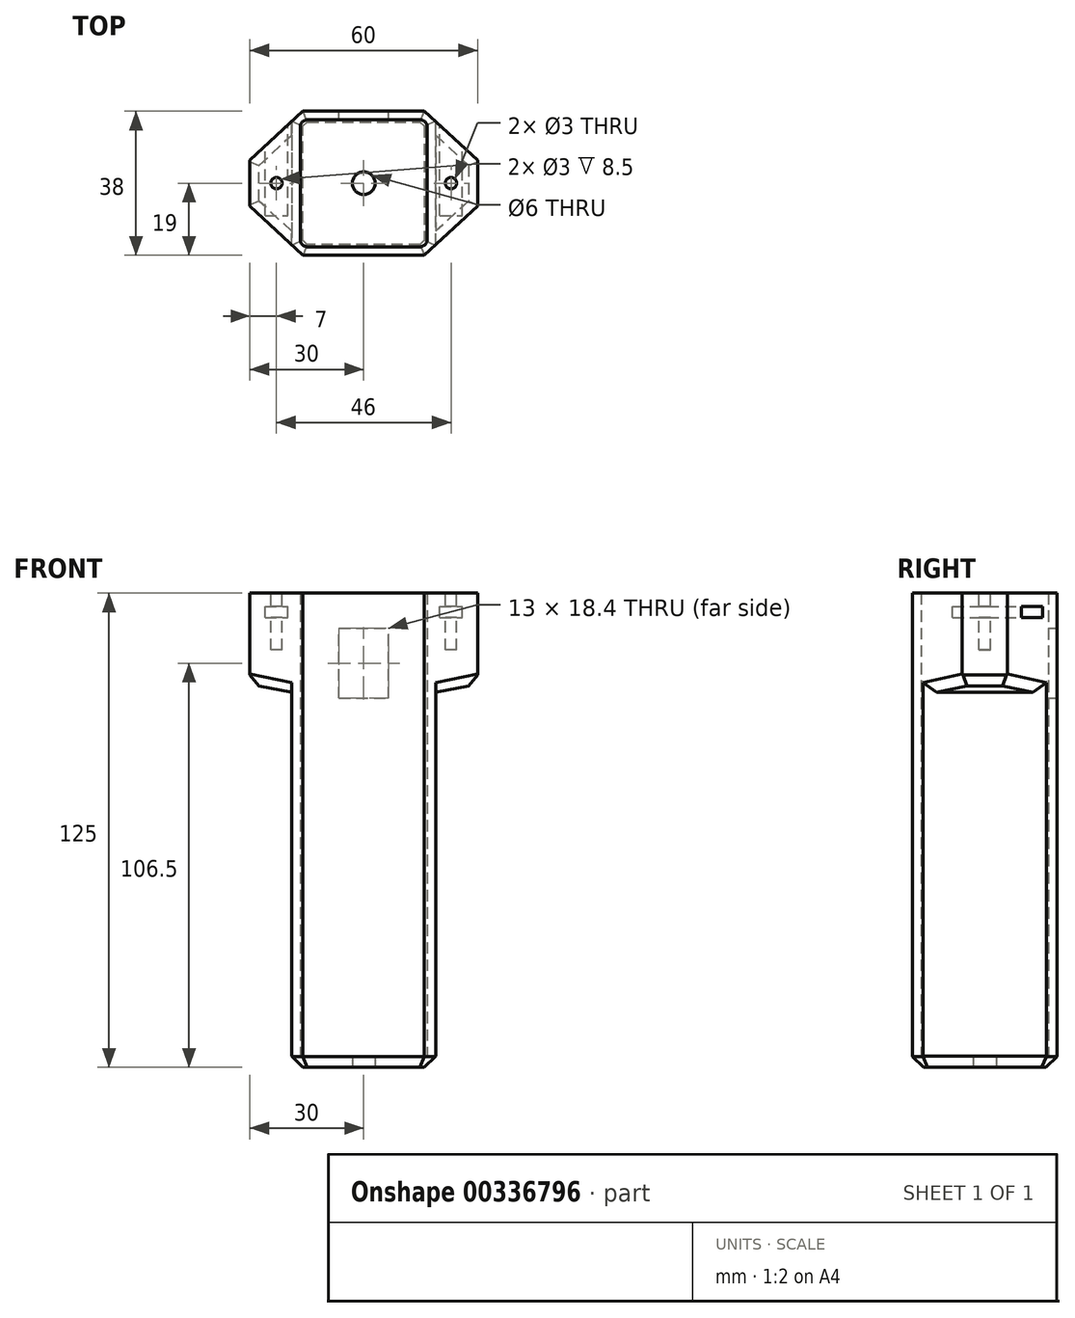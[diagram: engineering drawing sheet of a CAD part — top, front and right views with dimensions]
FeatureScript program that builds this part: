
annotation { "Feature Type Name" : "Feature", "Feature Type Description" : "" }
export const myFeature = defineFeature(function(context is Context, id is Id, definition is map)
    precondition{}
    {
        {
            var Q0;
            Q0=qCreatedBy(makeId("Top.planeOp"),FACE);
            var sketch = newSketch(context, id + "F0", { "sketchPlane" : qUnion([Q0])});
            skLineSegment(sketch, "E0.bottom", {"start": v(14.75, -16.75) * mm, "end": v(-14.75, -16.75) * mm});
            skLineSegment(sketch, "E0.top", {"start": v(14.75, 16.75) * mm, "end": v(-14.75, 16.75) * mm});
            skLineSegment(sketch, "E0.left", {"start": v(16.75, -14.75) * mm, "end": v(16.75, 14.75) * mm});
            skLineSegment(sketch, "E0.right", {"start": v(-16.75, -14.75) * mm, "end": v(-16.75, 14.75) * mm});
            skPoint(sketch, "E0.middle", {"position": v(0, 0) * mm});
            skLineSegment(sketch, "E1", {"start": v(-16, -19) * mm, "end": v(-30, -6) * mm});
            skLineSegment(sketch, "E2", {"start": v(-30, 6) * mm, "end": v(-16, 19) * mm});
            skLineSegment(sketch, "E3", {"start": v(16, 19) * mm, "end": v(30, 6) * mm});
            skLineSegment(sketch, "E4", {"start": v(30, -6) * mm, "end": v(16, -19) * mm});
            skLineSegment(sketch, "E5", {"start": v(-16, -19) * mm, "end": v(16, -19) * mm});
            skLineSegment(sketch, "E6", {"start": v(-30, -6) * mm, "end": v(-30, 6) * mm});
            skLineSegment(sketch, "E7", {"start": v(30, -6) * mm, "end": v(30, 6) * mm});
            skLineSegment(sketch, "E8", {"start": v(16, 19) * mm, "end": v(-16, 19) * mm});
            skPoint(sketch, "E9.visualSharp", {"position": v(-16.75, 16.75) * mm});
            skArc(sketch, "E9.filletArc", {"start": v(-14.75, 16.75) * mm, "mid": v(-16.16, 16.16) * mm, "end": v(-16.75, 14.75) * mm});
            skPoint(sketch, "E10.visualSharp", {"position": v(16.75, 16.75) * mm});
            skArc(sketch, "E10.filletArc", {"start": v(16.75, 14.75) * mm, "mid": v(16.16, 16.16) * mm, "end": v(14.75, 16.75) * mm});
            skPoint(sketch, "E11.visualSharp", {"position": v(16.75, -16.75) * mm});
            skArc(sketch, "E11.filletArc", {"start": v(14.75, -16.75) * mm, "mid": v(16.16, -16.16) * mm, "end": v(16.75, -14.75) * mm});
            skPoint(sketch, "E12.visualSharp", {"position": v(-16.75, -16.75) * mm});
            skArc(sketch, "E12.filletArc", {"start": v(-16.75, -14.75) * mm, "mid": v(-16.16, -16.16) * mm, "end": v(-14.75, -16.75) * mm});
            skSolve(sketch);
        }
        {
            var Q0;
            Q0 = qSketchRegion(id + "F0", true);
            extrude(context, id + "F1", {"entities" : qUnion([Q0]), "depth" : 115 * mm});
        }
        {
            var Q0;
            Q0=makeQuery(id+"F1.opExtrude","CAP_FACE",FACE,{"disambiguationData":[OSD([sQuery(id+"F0.wireOp",EDGE,"E0.bottom"),sQuery(id+"F0.wireOp",EDGE,"E0.top"),sQuery(id+"F0.wireOp",EDGE,"E0.left"),sQuery(id+"F0.wireOp",EDGE,"E0.right"),sQuery(id+"F0.wireOp",EDGE,"E1"),sQuery(id+"F0.wireOp",EDGE,"E2"),sQuery(id+"F0.wireOp",EDGE,"E3"),sQuery(id+"F0.wireOp",EDGE,"E4"),sQuery(id+"F0.wireOp",EDGE,"E5"),sQuery(id+"F0.wireOp",EDGE,"E6"),sQuery(id+"F0.wireOp",EDGE,"E7"),sQuery(id+"F0.wireOp",EDGE,"E8"),sQuery(id+"F0.wireOp",EDGE,"E9.filletArc"),sQuery(id+"F0.wireOp",EDGE,"E10.filletArc"),sQuery(id+"F0.wireOp",EDGE,"E11.filletArc"),sQuery(id+"F0.wireOp",EDGE,"E12.filletArc")])],"isStart":true});
            var sketch = newSketch(context, id + "F2", { "sketchPlane" : qUnion([Q0])});
            skLineSegment(sketch, "E13", {"start": v(16, 19) * mm, "end": v(30, 6) * mm});
            skLineSegment(sketch, "E14", {"start": v(30, 6) * mm, "end": v(30, -6) * mm});
            skLineSegment(sketch, "E15", {"start": v(30, -6) * mm, "end": v(16, -19) * mm});
            skLineSegment(sketch, "E16", {"start": v(16, -19) * mm, "end": v(-16, -19) * mm});
            skLineSegment(sketch, "E17", {"start": v(-16, -19) * mm, "end": v(-30, -6) * mm});
            skLineSegment(sketch, "E18", {"start": v(-30, -6) * mm, "end": v(-30, 6) * mm});
            skLineSegment(sketch, "E19", {"start": v(-30, 6) * mm, "end": v(-16, 19) * mm});
            skLineSegment(sketch, "E20", {"start": v(-16, 19) * mm, "end": v(16, 19) * mm});
            skSolve(sketch);
        }
        {
            var Q0;
            Q0 = qSketchRegion(id + "F2", true);
            var Q1;
            Q1 = qSketchRegion(id + "F4", true);
            extrude(context, id + "F3", {"entities" : qUnion([Q0, Q1]), "operationType" : NewBodyOperationType.ADD, "depth" : 10 * mm});
        }
        {
            var Q0;
            Q0=makeQuery(id+"F3.opExtrude","CAP_FACE",FACE,{"disambiguationData":[OSD([sQuery(id+"F2.wireOp",EDGE,"E13"),sQuery(id+"F2.wireOp",EDGE,"E14"),sQuery(id+"F2.wireOp",EDGE,"E15"),sQuery(id+"F2.wireOp",EDGE,"E16"),sQuery(id+"F2.wireOp",EDGE,"E17"),sQuery(id+"F2.wireOp",EDGE,"E18"),sQuery(id+"F2.wireOp",EDGE,"E19"),sQuery(id+"F2.wireOp",EDGE,"E20")])],"isStart":false});
            var sketch = newSketch(context, id + "F4", { "sketchPlane" : qUnion([Q0])});
            skCircle(sketch, "E21", {"center": v(0, 0) * mm, "radius": 3 * mm});
            skSolve(sketch);
        }
        {
            var Q0;
            Q0 = qSketchRegion(id + "F4", true);
            extrude(context, id + "F5", {"entities" : qUnion([Q0]), "operationType" : NewBodyOperationType.REMOVE, "oppositeDirection" : true, "depth" : 25 * mm});
        }
        {
            var Q0;
            Q0=makeQuery(id+"F1.opExtrude","CAP_FACE",FACE,{"disambiguationData":[OSD([sQuery(id+"F0.wireOp",EDGE,"E0.bottom"),sQuery(id+"F0.wireOp",EDGE,"E0.top"),sQuery(id+"F0.wireOp",EDGE,"E0.left"),sQuery(id+"F0.wireOp",EDGE,"E0.right"),sQuery(id+"F0.wireOp",EDGE,"E1"),sQuery(id+"F0.wireOp",EDGE,"E2"),sQuery(id+"F0.wireOp",EDGE,"E3"),sQuery(id+"F0.wireOp",EDGE,"E4"),sQuery(id+"F0.wireOp",EDGE,"E5"),sQuery(id+"F0.wireOp",EDGE,"E6"),sQuery(id+"F0.wireOp",EDGE,"E7"),sQuery(id+"F0.wireOp",EDGE,"E8"),sQuery(id+"F0.wireOp",EDGE,"E9.filletArc"),sQuery(id+"F0.wireOp",EDGE,"E10.filletArc"),sQuery(id+"F0.wireOp",EDGE,"E11.filletArc"),sQuery(id+"F0.wireOp",EDGE,"E12.filletArc")])],"isStart":false});
            var sketch = newSketch(context, id + "F6", { "sketchPlane" : qUnion([Q0])});
            skLineSegment(sketch, "E22", {"start": v(-30, -6) * mm, "end": v(-30, 6) * mm});
            skLineSegment(sketch, "E23", {"start": v(-30, 6) * mm, "end": v(-16, 19) * mm});
            skLineSegment(sketch, "E24", {"start": v(-16, 19) * mm, "end": v(16, 19) * mm});
            skLineSegment(sketch, "E25", {"start": v(16, 19) * mm, "end": v(30, 6) * mm});
            skLineSegment(sketch, "E26", {"start": v(30, 6) * mm, "end": v(30, -6) * mm});
            skLineSegment(sketch, "E27", {"start": v(30, -6) * mm, "end": v(16, -19) * mm});
            skLineSegment(sketch, "E28", {"start": v(16, -19) * mm, "end": v(-16, -19) * mm});
            skLineSegment(sketch, "E29", {"start": v(-16, -19) * mm, "end": v(-30, -6) * mm});
            skSolve(sketch);
        }
        {
            var Q0;
            Q0=makeQuery(id+"F6.imprint","IMPRINT",FACE,{"disambiguationData":[TD([[makeQuery(id+"F6.imprint","IMPRINT",EDGE,{"derivedFrom":sQuery(id+"F6.wireOp",EDGE,"E22")}),-1.0]])]});
            var sketch = newSketch(context, id + "F7", { "sketchPlane" : qUnion([Q0])});
            skPoint(sketch, "E30.middle", {"position": v(0, 0) * mm});
            skCircle(sketch, "E31", {"center": v(23, 0) * mm, "radius": 1.5 * mm});
            skCircle(sketch, "E32", {"center": v(-23, 0) * mm, "radius": 1.5 * mm});
            skLineSegment(sketch, "E33.bottom", {"start": v(-23, 0) * mm, "end": v(23, 0) * mm});
            skLineSegment(sketch, "E33.top", {"start": v(-23, 19.77) * mm, "end": v(23, 19.77) * mm});
            skLineSegment(sketch, "E33.left", {"start": v(-23, 0) * mm, "end": v(-23, 19.77) * mm});
            skLineSegment(sketch, "E33.right", {"start": v(23, 0) * mm, "end": v(23, 19.77) * mm});
            skSolve(sketch);
        }
        {
            var Q0;
            Q0=makeQuery(id+"F7.imprint","IMPRINT",FACE,{"disambiguationData":[TD([[makeQuery(id+"F7.imprint","IMPRINT",EDGE,{"derivedFrom":sQuery(id+"F7.wireOp",EDGE,"E31")}),1.0]])]});
            var Q1;
            Q1=makeQuery(id+"F7.imprint","IMPRINT",FACE,{"disambiguationData":[TD([[makeQuery(id+"F7.imprint","IMPRINT",EDGE,{"derivedFrom":sQuery(id+"F7.wireOp",EDGE,"E32")}),1.0]])]});
            var Q2;
            Q2=sQuery(id+"F7.wireOp",EDGE,"E31");
            var Q3;
            Q3=sQuery(id+"F7.wireOp",EDGE,"E32");
            extrude(context, id + "F8", {"entities" : qUnion([Q0, Q1]), "operationType" : NewBodyOperationType.REMOVE, "surfaceEntities" : qUnion([Q2, Q3]), "oppositeDirection" : true, "depth" : 15 * mm});
        }
        {
            var Q0;
            Q0=makeQuery(id+"F3.opExtrude","CAP_EDGE",EDGE,{"disambiguationData":[OSD([sQuery(id+"F2.wireOp",EDGE,"E16")])],"isStart":false});
            var Q1;
            Q1=makeQuery(id+"F3.opExtrude","CAP_EDGE",EDGE,{"disambiguationData":[OSD([sQuery(id+"F2.wireOp",EDGE,"E17")])],"isStart":false});
            var Q2;
            Q2=makeQuery(id+"F3.opExtrude","CAP_EDGE",EDGE,{"disambiguationData":[OSD([sQuery(id+"F2.wireOp",EDGE,"E15")])],"isStart":false});
            var Q3;
            Q3=makeQuery(id+"F3.opExtrude","CAP_EDGE",EDGE,{"disambiguationData":[OSD([sQuery(id+"F2.wireOp",EDGE,"E13")])],"isStart":false});
            var Q4;
            Q4=makeQuery(id+"F3.opExtrude","CAP_EDGE",EDGE,{"disambiguationData":[OSD([sQuery(id+"F2.wireOp",EDGE,"E20")])],"isStart":false});
            var Q5;
            Q5=makeQuery(id+"F3.opExtrude","CAP_EDGE",EDGE,{"disambiguationData":[OSD([sQuery(id+"F2.wireOp",EDGE,"E19")])],"isStart":false});
            var Q6;
            Q6=makeQuery(id+"F3.opExtrude","CAP_EDGE",EDGE,{"disambiguationData":[OSD([sQuery(id+"F2.wireOp",EDGE,"E18")])],"isStart":false});
            var Q7;
            Q7=makeQuery(id+"F3.opExtrude","CAP_EDGE",EDGE,{"disambiguationData":[OSD([sQuery(id+"F2.wireOp",EDGE,"E14")])],"isStart":false});
            chamfer(context, id + "F9", {"entities" : qUnion([Q0, Q1, Q2, Q3, Q4, Q5, Q6, Q7]), "width" : 2.9 * mm, "tangentPropagation" : true});
        }
        {
            var Q0;
            Q0=makeQuery(id+"F3.boolean.opBoolean","MERGE",FACE,{"derivedFrom":[makeQuery(id+"F1.opExtrude","SWEPT_FACE",FACE,{"disambiguationData":[OSD([sQuery(id+"F0.wireOp",EDGE,"E5")])]}),makeQuery(id+"F3.opExtrude","SWEPT_FACE",FACE,{"disambiguationData":[OSD([sQuery(id+"F2.wireOp",EDGE,"E20")])]})]});
            var sketch = newSketch(context, id + "F10", { "sketchPlane" : qUnion([Q0])});
            skLineSegment(sketch, "E34", {"start": v(0, 115) * mm, "end": v(0, 95) * mm});
            skPoint(sketch, "E34.endSnap0", {"position": v(0, 115) * mm});
            skPoint(sketch, "E35.middle", {"position": v(0, 95) * mm});
            skLineSegment(sketch, "E36", {"start": v(0, 85) * mm, "end": v(-50, 95) * mm});
            skLineSegment(sketch, "E37", {"start": v(0, 85) * mm, "end": v(50, 95) * mm});
            skPoint(sketch, "E38.middle", {"position": v(0, 85) * mm});
            skPoint(sketch, "E39.middle", {"position": v(12.9, 75) * mm});
            skLineSegment(sketch, "E40", {"start": v(19, 75) * mm, "end": v(19, 88.8) * mm});
            skLineSegment(sketch, "E41", {"start": v(-19, 75) * mm, "end": v(-19, 88.8) * mm});
            skLineSegment(sketch, "E42", {"start": v(19, 75) * mm, "end": v(19, -17.44) * mm});
            skLineSegment(sketch, "E43", {"start": v(-19, 75) * mm, "end": v(-19, -15.08) * mm});
            skLineSegment(sketch, "E44", {"start": v(-19, -15.08) * mm, "end": v(-58.81, -15.08) * mm});
            skLineSegment(sketch, "E45", {"start": v(-58.81, -15.08) * mm, "end": v(-73.57, 132.3) * mm});
            skLineSegment(sketch, "E46", {"start": v(58.57, 145.53) * mm, "end": v(83.51, 80.11) * mm});
            skLineSegment(sketch, "E47", {"start": v(83.51, 80.11) * mm, "end": v(61.9, -31.11) * mm});
            skLineSegment(sketch, "E48", {"start": v(61.9, -31.11) * mm, "end": v(19, -17.44) * mm});
            skLineSegment(sketch, "E49", {"start": v(-73.57, 132.3) * mm, "end": v(-50, 95) * mm});
            skLineSegment(sketch, "E50", {"start": v(50, 95) * mm, "end": v(58.57, 145.53) * mm});
            skSolve(sketch);
        }
        {
            var Q0;
            Q0 = qSketchRegion(id + "F10", true);
            extrude(context, id + "F11", {"entities" : qUnion([Q0]), "operationType" : NewBodyOperationType.REMOVE, "oppositeDirection" : true, "depth" : 50 * mm, "hasSecondDirection" : true, "secondDirectionOppositeDirection" : false, "secondDirectionDepth" : 25 * mm});
        }
        {
            var Q0;
            Q0=makeQuery(id+"F11.boolean.opBoolean","INTERSECT",EDGE,{"derivedFrom":[makeQuery(id+"F3.opExtrude","CAP_FACE",FACE,{"disambiguationData":[OSD([sQuery(id+"F2.wireOp",EDGE,"E13"),sQuery(id+"F2.wireOp",EDGE,"E14"),sQuery(id+"F2.wireOp",EDGE,"E15"),sQuery(id+"F2.wireOp",EDGE,"E16"),sQuery(id+"F2.wireOp",EDGE,"E17"),sQuery(id+"F2.wireOp",EDGE,"E18"),sQuery(id+"F2.wireOp",EDGE,"E19"),sQuery(id+"F2.wireOp",EDGE,"E20")])],"isStart":false}),makeQuery(id+"F11.opExtrude","SWEPT_FACE",FACE,{"disambiguationData":[OSD([sQuery(id+"F10.wireOp",EDGE,"E40"),sQuery(id+"F10.wireOp",EDGE,"E42")])]})]});
            var Q1;
            Q1=makeQuery(id+"F11.boolean.opBoolean","INTERSECT",EDGE,{"derivedFrom":[makeQuery(id+"F3.opExtrude","CAP_FACE",FACE,{"disambiguationData":[OSD([sQuery(id+"F2.wireOp",EDGE,"E13"),sQuery(id+"F2.wireOp",EDGE,"E14"),sQuery(id+"F2.wireOp",EDGE,"E15"),sQuery(id+"F2.wireOp",EDGE,"E16"),sQuery(id+"F2.wireOp",EDGE,"E17"),sQuery(id+"F2.wireOp",EDGE,"E18"),sQuery(id+"F2.wireOp",EDGE,"E19"),sQuery(id+"F2.wireOp",EDGE,"E20")])],"isStart":false}),makeQuery(id+"F11.opExtrude","SWEPT_FACE",FACE,{"disambiguationData":[OSD([sQuery(id+"F10.wireOp",EDGE,"E41"),sQuery(id+"F10.wireOp",EDGE,"E43")])]})]});
            chamfer(context, id + "F12", {"entities" : qUnion([Q0, Q1]), "width" : 3 * mm, "tangentPropagation" : true});
        }
        {
            var Q0;
            Q0=makeQuery(id+"F11.boolean.opBoolean","INTERSECT",EDGE,{"derivedFrom":[makeQuery(id+"F3.boolean.opBoolean","MERGE",FACE,{"derivedFrom":[makeQuery(id+"F1.opExtrude","SWEPT_FACE",FACE,{"disambiguationData":[OSD([sQuery(id+"F0.wireOp",EDGE,"E1")])]}),makeQuery(id+"F3.opExtrude","SWEPT_FACE",FACE,{"disambiguationData":[OSD([sQuery(id+"F2.wireOp",EDGE,"E19")])]})]}),makeQuery(id+"F11.opExtrude","SWEPT_FACE",FACE,{"disambiguationData":[OSD([sQuery(id+"F10.wireOp",EDGE,"E36")])]})]});
            var Q1;
            Q1=makeQuery(id+"F11.boolean.opBoolean","INTERSECT",EDGE,{"derivedFrom":[makeQuery(id+"F3.boolean.opBoolean","MERGE",FACE,{"derivedFrom":[makeQuery(id+"F1.opExtrude","SWEPT_FACE",FACE,{"disambiguationData":[OSD([sQuery(id+"F0.wireOp",EDGE,"E2")])]}),makeQuery(id+"F3.opExtrude","SWEPT_FACE",FACE,{"disambiguationData":[OSD([sQuery(id+"F2.wireOp",EDGE,"E17")])]})]}),makeQuery(id+"F11.opExtrude","SWEPT_FACE",FACE,{"disambiguationData":[OSD([sQuery(id+"F10.wireOp",EDGE,"E36")])]})]});
            var Q2;
            Q2=makeQuery(id+"F11.boolean.opBoolean","INTERSECT",EDGE,{"derivedFrom":[makeQuery(id+"F3.boolean.opBoolean","MERGE",FACE,{"derivedFrom":[makeQuery(id+"F1.opExtrude","SWEPT_FACE",FACE,{"disambiguationData":[OSD([sQuery(id+"F0.wireOp",EDGE,"E4")])]}),makeQuery(id+"F3.opExtrude","SWEPT_FACE",FACE,{"disambiguationData":[OSD([sQuery(id+"F2.wireOp",EDGE,"E13")])]})]}),makeQuery(id+"F11.opExtrude","SWEPT_FACE",FACE,{"disambiguationData":[OSD([sQuery(id+"F10.wireOp",EDGE,"E37")])]})]});
            var Q3;
            Q3=makeQuery(id+"F11.boolean.opBoolean","INTERSECT",EDGE,{"derivedFrom":[makeQuery(id+"F3.boolean.opBoolean","MERGE",FACE,{"derivedFrom":[makeQuery(id+"F1.opExtrude","SWEPT_FACE",FACE,{"disambiguationData":[OSD([sQuery(id+"F0.wireOp",EDGE,"E3")])]}),makeQuery(id+"F3.opExtrude","SWEPT_FACE",FACE,{"disambiguationData":[OSD([sQuery(id+"F2.wireOp",EDGE,"E15")])]})]}),makeQuery(id+"F11.opExtrude","SWEPT_FACE",FACE,{"disambiguationData":[OSD([sQuery(id+"F10.wireOp",EDGE,"E37")])]})]});
            var Q4;
            Q4=makeQuery(id+"F11.boolean.opBoolean","INTERSECT",EDGE,{"derivedFrom":[makeQuery(id+"F3.boolean.opBoolean","MERGE",FACE,{"derivedFrom":[makeQuery(id+"F1.opExtrude","SWEPT_FACE",FACE,{"disambiguationData":[OSD([sQuery(id+"F0.wireOp",EDGE,"E7")])]}),makeQuery(id+"F3.opExtrude","SWEPT_FACE",FACE,{"disambiguationData":[OSD([sQuery(id+"F2.wireOp",EDGE,"E14")])]})]}),makeQuery(id+"F11.opExtrude","SWEPT_FACE",FACE,{"disambiguationData":[OSD([sQuery(id+"F10.wireOp",EDGE,"E37")])]})]});
            var Q5;
            Q5=makeQuery(id+"F11.boolean.opBoolean","INTERSECT",EDGE,{"derivedFrom":[makeQuery(id+"F3.boolean.opBoolean","MERGE",FACE,{"derivedFrom":[makeQuery(id+"F1.opExtrude","SWEPT_FACE",FACE,{"disambiguationData":[OSD([sQuery(id+"F0.wireOp",EDGE,"E6")])]}),makeQuery(id+"F3.opExtrude","SWEPT_FACE",FACE,{"disambiguationData":[OSD([sQuery(id+"F2.wireOp",EDGE,"E18")])]})]}),makeQuery(id+"F11.opExtrude","SWEPT_FACE",FACE,{"disambiguationData":[OSD([sQuery(id+"F10.wireOp",EDGE,"E36")])]})]});
            chamfer(context, id + "F13", {"entities" : qUnion([Q0, Q1, Q2, Q3, Q4, Q5]), "width" : 3 * mm, "tangentPropagation" : true});
        }
        {
            var Q0;
            Q0=makeQuery(id+"F1.opExtrude","CAP_FACE",FACE,{"disambiguationData":[OSD([sQuery(id+"F0.wireOp",EDGE,"E0.bottom"),sQuery(id+"F0.wireOp",EDGE,"E0.top"),sQuery(id+"F0.wireOp",EDGE,"E0.left"),sQuery(id+"F0.wireOp",EDGE,"E0.right"),sQuery(id+"F0.wireOp",EDGE,"E1"),sQuery(id+"F0.wireOp",EDGE,"E2"),sQuery(id+"F0.wireOp",EDGE,"E3"),sQuery(id+"F0.wireOp",EDGE,"E4"),sQuery(id+"F0.wireOp",EDGE,"E5"),sQuery(id+"F0.wireOp",EDGE,"E6"),sQuery(id+"F0.wireOp",EDGE,"E7"),sQuery(id+"F0.wireOp",EDGE,"E8"),sQuery(id+"F0.wireOp",EDGE,"E9.filletArc"),sQuery(id+"F0.wireOp",EDGE,"E10.filletArc"),sQuery(id+"F0.wireOp",EDGE,"E11.filletArc"),sQuery(id+"F0.wireOp",EDGE,"E12.filletArc")])],"isStart":false});
            var sketch = newSketch(context, id + "F14", { "sketchPlane" : qUnion([Q0])});
            skSolve(sketch);
        }
        {
            var Q0;
            Q0=makeQuery(id+"F3.boolean.opBoolean","MERGE",FACE,{"derivedFrom":[makeQuery(id+"F1.opExtrude","SWEPT_FACE",FACE,{"disambiguationData":[OSD([sQuery(id+"F0.wireOp",EDGE,"E8")])]}),makeQuery(id+"F3.opExtrude","SWEPT_FACE",FACE,{"disambiguationData":[OSD([sQuery(id+"F2.wireOp",EDGE,"E16")])]})]});
            var sketch = newSketch(context, id + "F15", { "sketchPlane" : qUnion([Q0])});
            skLineSegment(sketch, "E51.left", {"start": v(23, 110) * mm, "end": v(23, 111.5) * mm});
            skLineSegment(sketch, "E51.right", {"start": v(-23, 110) * mm, "end": v(-23, 111.5) * mm});
            skPoint(sketch, "E51.middle", {"position": v(0, 115) * mm});
            skLineSegment(sketch, "E52.bottom", {"start": v(-20, 108.5) * mm, "end": v(-26, 108.5) * mm});
            skLineSegment(sketch, "E52.top", {"start": v(-20, 111.5) * mm, "end": v(-26, 111.5) * mm});
            skLineSegment(sketch, "E52.left", {"start": v(-20, 108.5) * mm, "end": v(-20, 111.5) * mm});
            skLineSegment(sketch, "E52.right", {"start": v(-26, 108.5) * mm, "end": v(-26, 111.5) * mm});
            skPoint(sketch, "E52.middle", {"position": v(-23, 110) * mm});
            skLineSegment(sketch, "E53.bottom", {"start": v(26, 108.5) * mm, "end": v(20, 108.5) * mm});
            skLineSegment(sketch, "E53.top", {"start": v(26, 111.5) * mm, "end": v(20, 111.5) * mm});
            skLineSegment(sketch, "E53.left", {"start": v(26, 108.5) * mm, "end": v(26, 111.5) * mm});
            skLineSegment(sketch, "E53.right", {"start": v(20, 108.5) * mm, "end": v(20, 111.5) * mm});
            skPoint(sketch, "E53.middle", {"position": v(23, 110) * mm});
            skPoint(sketch, "E51.top.start.orphan", {"position": v(23, 120) * mm});
            skPoint(sketch, "E54.orphan", {"position": v(-23, 120) * mm});
            skSolve(sketch);
        }
        {
            var Q0;
            Q0 = qSketchRegion(id + "F15", true);
            extrude(context, id + "F16", {"entities" : qUnion([Q0]), "operationType" : NewBodyOperationType.REMOVE, "oppositeDirection" : true, "depth" : 27.5 * mm});
        }
        {
            var Q0;
            Q0=makeQuery(id+"F14.imprint","IMPRINT",FACE,{"disambiguationData":[TD([[makeQuery(id+"F14.imprint","IMPRINT",EDGE,{"derivedFrom":makeQuery(id+"F1.opExtrude","CAP_EDGE",EDGE,{"disambiguationData":[OSD([sQuery(id+"F0.wireOp",EDGE,"E0.bottom")])],"isStart":false})}),-1.0]])]});
            extrude(context, id + "F17", {"entities" : qUnion([Q0]), "operationType" : NewBodyOperationType.REMOVE, "oppositeDirection" : true, "depth" : 122 * mm});
        }
        {
            var Q0;
            Q0=makeQuery(id+"F3.boolean.opBoolean","MERGE",FACE,{"derivedFrom":[makeQuery(id+"F1.opExtrude","SWEPT_FACE",FACE,{"disambiguationData":[OSD([sQuery(id+"F0.wireOp",EDGE,"E8")])]}),makeQuery(id+"F3.opExtrude","SWEPT_FACE",FACE,{"disambiguationData":[OSD([sQuery(id+"F2.wireOp",EDGE,"E16")])]})]});
            var sketch = newSketch(context, id + "F18", { "sketchPlane" : qUnion([Q0])});
            skLineSegment(sketch, "E55", {"start": v(0, 115) * mm, "end": v(0, 105) * mm});
            skPoint(sketch, "E55.endSnap0", {"position": v(0, 115) * mm});
            skLineSegment(sketch, "E56", {"start": v(0, 105) * mm, "end": v(0, 96.5) * mm});
            skPoint(sketch, "E57.middle", {"position": v(0, 96.5) * mm});
            skLineSegment(sketch, "E58.bottom", {"start": v(6.5, 87.3) * mm, "end": v(-6.5, 87.3) * mm});
            skLineSegment(sketch, "E58.top", {"start": v(6.5, 105.7) * mm, "end": v(-6.5, 105.7) * mm});
            skLineSegment(sketch, "E58.left", {"start": v(6.5, 87.3) * mm, "end": v(6.5, 105.7) * mm});
            skLineSegment(sketch, "E58.right", {"start": v(-6.5, 87.3) * mm, "end": v(-6.5, 105.7) * mm});
            skSolve(sketch);
        }
        {
            var Q0;
            Q0 = qSketchRegion(id + "F18", true);
            extrude(context, id + "F19", {"entities" : qUnion([Q0]), "operationType" : NewBodyOperationType.REMOVE, "oppositeDirection" : true, "depth" : 25 * mm});
        }
    });
